# Revit family: WCSeat&Cover-Duroplast-SoftClosing-TopFixing-QuickRelease-Vitra-PluralSeries_126
name_source: partatom
category: Plumbing Fixtures
revit_build: Autodesk Revit 2017 (Build: 20160225_1515(x64)
units: mm (PartAtom-declared; Revit-internal decimal feet)

## family parameters
Cut with Voids When Loaded = No
Host = Face
OmniClass Number = 23.45.05.00
OmniClass Title = Sanitary Equipment
Part Type = Normal
Room Calculation Point = No
Round Connector Dimension = Use Diameter
Shared = Yes

## types (15) — shared parameters
BIMobject category = Sanitary - Toilet Seats
Brand = VitrA
CW Connection = No
Default Elevation = 410 mm  [stored 1.34514 ft]
Description = VitrA Plural WC Seat, Soft Closing, top fixing, quick release
Design country = Turkey
HW Connection = No
IFC Classification = Sanitary Terminal
Main Material = Duroplast
Manufacturer = Vitra
Manufacturer name = Vitra
NBS Referans Code = 35-93-95
NBS Referans Description = Wc Seats And Covers
Nominal Depth (mm) = 478 mm  [stored 1.56824 ft]
Nominal Height (mm) = 50 mm  [stored 0.164042 ft]
Nominal Width (mm) = 366 mm
OmniClass Code = 23-31 19 19 11
OmniClass Description = Toilets
Product certification = https://www.vitraglobal.com
Product family = Plural
Technical description = https://www.vitraglobal.com
UNSPSC Code = 35-93-95
UNSPSC Description = Water Operated Water Closets
URL = https://www.vitra.com.tr
Uniclass 1.4 Code = L72164
Uniclass 1.4 Description = Toilets
Uniclass 2.0 Code = PR-35-93-95
Uniclass 2.0 Description = Wc Seats And Covers
Uniclass 2015 Code = Pr_40_20_93_95
Uniclass 2015 Name = WC seats and covers
Vent Connection = No
Warranty Period (Year) = 2 Years
Waste Connection = No
Weight Net (kg) = 2.2
Youtube = https://www.youtube.com

## per-type parameters (varying)
| type | Article No. (default) | Color | Model | Primary Material | Product SKU | Product data url | Product url | Secondary Material |
| WCSeat&Cover-Duroplast-CopperMetalHinge-SoftClosing-TopFixing-QuickRelease-Vitra-PluralSeries(MatteBlack)-126-083-029 | 126-083-029 | Matte Black | 126-083-029 | MatteBlack-WCSeat | 126-083-029 | https://www.vitraglobal.com | https://www.vitraglobal.com | BrightCopper |
| WCSeat&Cover-Duroplast-CopperMetalHinge-SoftClosing-TopFixing-QuickRelease-Vitra-PluralSeries(MatteMink)-126-050-029 | 126-050-029 | Matte Mink | 126-050-029 | MatteMink-WCSeat | 126-050-029 | https://www.vitraglobal.com | https://www.vitraglobal.com | BrightCopper |
| WCSeat&Cover-Duroplast-CopperMetalHinge-SoftClosing-TopFixing-QuickRelease-Vitra-PluralSeries(MatteBeige)-126-020-029 | 126-020-029 | Matte Beige | 126-020-029 | MatteTaupe-WCSeat | 126-020-029 | https://www.vitraglobal.com | https://www.vitraglobal.com | BrightCopper |
| WCSeat&Cover-Duroplast-CopperMetalHinge-SoftClosing-TopFixing-QuickRelease-Vitra-PluralSeries(MatteWhite)-126-001-029 | 126-001-029 | Matte White | 126-001-029 | MatteWhite-WCSeat | 126-001-029 | https://www.vitraglobal.com | https://www.vitraglobal.com | BrightCopper |
| WCSeat&Cover-Duroplast-CopperMetalHinge-SoftClosing-TopFixing-QuickRelease-Vitra-PluralSeries(White)-126-003-029 | 126-003-029 | White | 126-003-029 | White-WCSeat | 126-003-029 | https://www.vitraglobal.com | https://www.vitraglobal.com | BrightCopper |
| WCSeat&Cover-Duroplast-GoldMetalHinge-SoftClosing-TopFixing-QuickRelease-Vitra-PluralSeries(MatteBlack)-126-083-019 | 126-083-019 | MatteBlack | 126-083-019 | MatteBlack-WCSeat | 126-083-019 | https://www.vitraglobal.com | https://www.vitraglobal.com | Gold |
| WCSeat&Cover-Duroplast-GoldMetalHinge-SoftClosing-TopFixing-QuickRelease-Vitra-PluralSeries(MatteMink)-126-050-019 | 126-050-019 | MatteMink | 126-050-019 | MatteMink-WCSeat | 126-050-019 | https://www.vitraglobal.com | https://www.vitraglobal.com | Gold |
| WCSeat&Cover-Duroplast-GoldMetalHinge-SoftClosing-TopFixing-QuickRelease-Vitra-PluralSeries(MatteBeige)-126-020-019 | 126-020-019 | MatteBeige | 126-020-019 | MatteTaupe-WCSeat | 126-020-019 | https://www.vitraglobal.com | https://www.vitraglobal.com | Gold |
| WCSeat&Cover-Duroplast-GoldMetalHinge-SoftClosing-TopFixing-QuickRelease-Vitra-PluralSeries(MatteWhite)-126-001-019 | 126-001-019 | MatteWhite | 126-001-019 | MatteWhite-WCSeat | 126-001-019 | https://www.vitraglobal.com | https://www.vitraglobal.com | Gold |
| WCSeat&Cover-Duroplast-GoldMetalHinge-SoftClosing-TopFixing-QuickRelease-Vitra-PluralSeries(White)-126-003-019 | 126-003-019 | White | 126-003-019 | White-WCSeat | 126-003-019 | https://www.vitraglobal.com | https://www.vitraglobal.com | Gold |
| WCSeat&Cover-Duroplast-MetalHinge-SoftClosing-TopFixing-QuickRelease-Vitra-PluralSeries(MatteBlack)-126-083-009 | 126-083-009 | Matte Black | 126-083-009 | MatteBlack-WCSeat | 126-083-009 | https://www.vitraglobal.com | https://www.vitraglobal.com | Metal |
| WCSeat&Cover-Duroplast-MetalHinge-SoftClosing-TopFixing-QuickRelease-Vitra-PluralSeries(MatteMink)-126-050-009 | 126-050-009 | Mink | 126-050-009 | MatteMink-WCSeat | 126-050-009 | https://www.vitraglobal.com | https://www.vitraglobal.com | Metal |
| WCSeat&Cover-Duroplast-MetalHinge-SoftClosing-TopFixing-QuickRelease-Vitra-PluralSeries(MatteBeige)-126-020-009 | 126-020-009 | Beige | 126-020-009 | MatteTaupe-WCSeat | 126-020-009 | https://www.vitraglobal.com | https://www.vitraglobal.com | Metal |
| WCSeat&Cover-Duroplast-MetalHinge-SoftClosing-TopFixing-QuickRelease-Vitra-PluralSeries(MatteWhite)-126-001-009 | 126-001-009 | MatteWhite | 126-001-009 | MatteWhite-WCSeat | 126-001-009 | https://www.vitraglobal.com | https://www.vitraglobal.com | Metal |
| WCSeat&Cover-Duroplast-MetalHinge-SoftClosing-TopFixing-QuickRelease-Vitra-PluralSeries(White)-126-003-009 | 126-003-009 | White | 126-003-009 | White-WCSeat | 126-003-009 | https://www.bimobject.com | https://www.vitra.com.tr | Metal |

note: [stored X ft] marks values corroborated as IEEE doubles in the binary element streams (Revit-internal decimal feet)

## geometry (parser evidence)
native form markers: Sweep x2
no freeform markers — native parametric forms only
